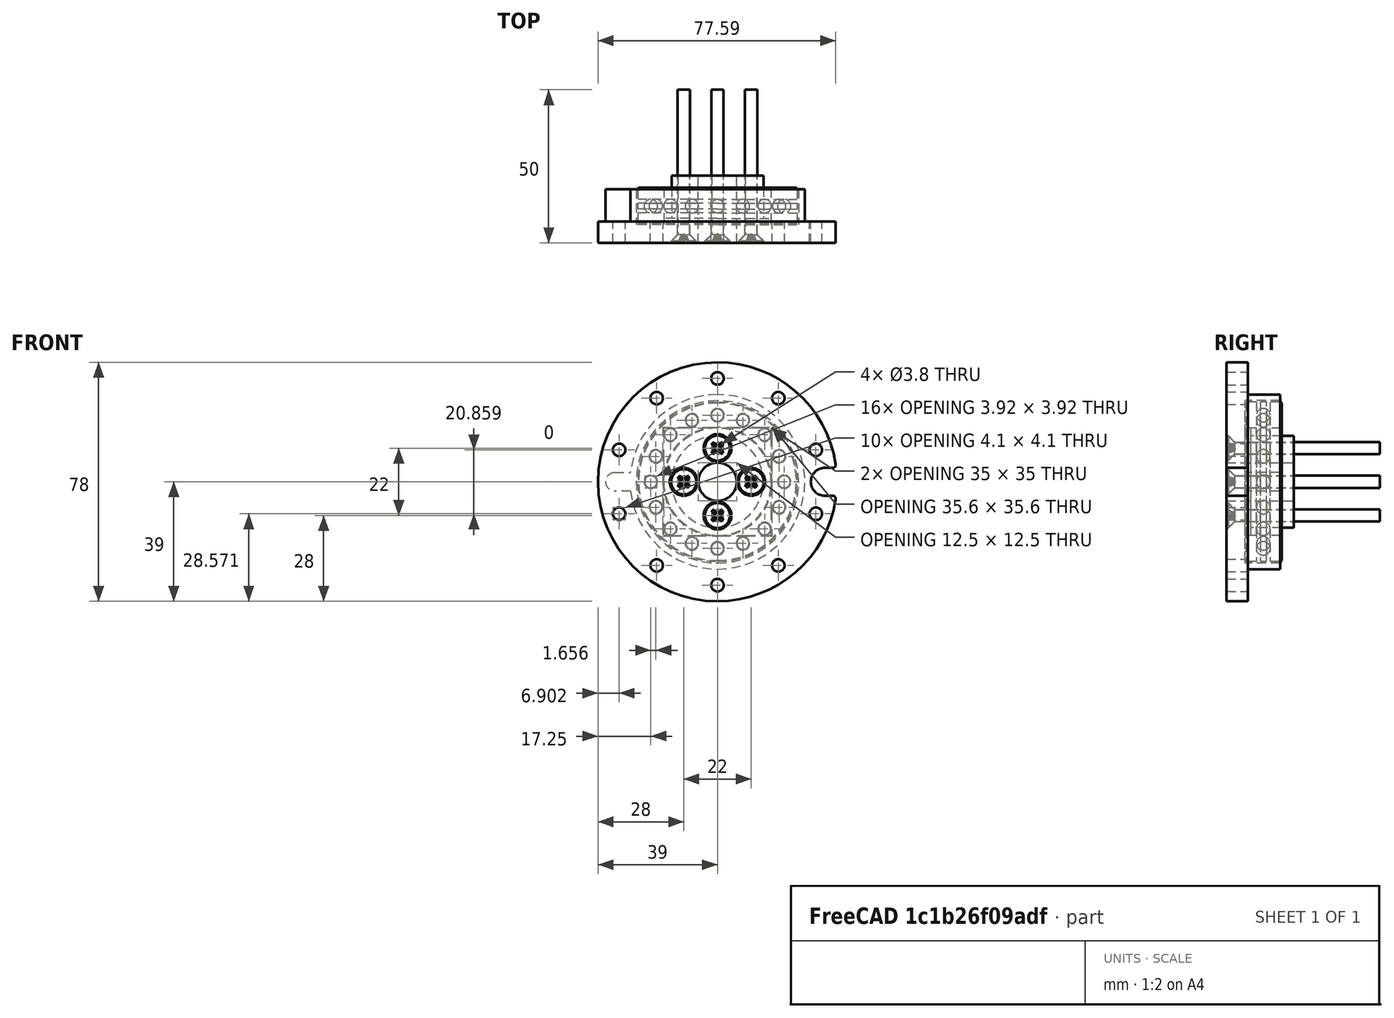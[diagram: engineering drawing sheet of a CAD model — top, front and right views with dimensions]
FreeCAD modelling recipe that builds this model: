
FCSTD DOCUMENT  (FreeCAD 0.19R)
Label: J3_a2p
License: All rights reserved
LicenseURL: http://en.wikipedia.org/wiki/All_rights_reserved
objects: Part::FeaturePython×6, App::FeaturePython×2, Spreadsheet::Sheet×2
note: 6 computed .brp shape members not serialized (recipe doc carries the construction recipe); baked Part::Feature solids carry a one-line shape summary decoded from their .brp

FEATURE [Part::FeaturePython] b_J3_coupler_modified_001_  label="J3_coupler_modified_001"  # a2plus imported part (geometry in sourceFile) (typed FeaturePython)
  a2p_Version = V0.1
  fixedPosition = true
  muxInfo = <blob: 8182 chars omitted>
  objectType = a2pPart
  sourceFile = ./J3_coupler_modified.FCStd
  subassemblyImport = false
  timeLastImport = 1.62025e+09
  updateColors = true
FEATURE [Part::FeaturePython] b_Thrust_bearing_511071_001_  label="Thrust_bearing_511071_001"  # a2plus imported part (geometry in sourceFile) (typed FeaturePython)
  Placement = pos=(-1.28618e-06,6,-2.39441e-06) rot=(0,0,1;0rad)
  a2p_Version = V0.1
  fixedPosition = false
  muxInfo = <blob: 16793 chars omitted>
  objectType = a2pPart
  sourceFile = ./Thrust_bearing_51107.step
  subassemblyImport = false
  timeLastImport = 1.62025e+09
  updateColors = true
FEATURE [App::FeaturePython] circularEdge_001  label="circularEdge_001__J3_coupler_modified_001"  # a2plus constraint (typed FeaturePython)
  Object1 = b_Thrust_bearing_511071_001_
  Object2 = b_J3_coupler_modified_001_
  ParentTreeObject = -> b_Thrust_bearing_511071_001_
  SubElement1 = Edge18
  SubElement2 = Edge157
  Suppressed = false
  Type = circularEdge
  directionConstraint = 1
  lockRotation = false
  offset = 0
FEATURE [App::FeaturePython] circularEdge_001_mirror  label="circularEdge_001__Thrust_bearing_511071_001"  # a2plus constraint (typed FeaturePython)
  Object1 = b_Thrust_bearing_511071_001_
  Object2 = b_J3_coupler_modified_001_
  ParentTreeObject = -> b_J3_coupler_modified_001_
  SubElement1 = Edge18
  SubElement2 = Edge157
  Suppressed = false
  Type = circularEdge
  directionConstraint = 1
  lockRotation = false
  offset = 0
FEATURE [Part::FeaturePython] Screw  label="M4x50-Screw"  # Fasteners workbench fastener (typed FeaturePython)
  Placement = pos=(0,-1.7e-15,-11) rot=(1,0,0;1.5708rad)
  baseObject = -> b_J3_coupler_modified_001_ [Edge46]
  diameter = 6
  invert = false
  length = 12
  lengthCustom = 50
  matchOuter = false
  offset = 0
  thread = false
  type = 35
FEATURE [Part::FeaturePython] Screw001  label="M4x50-Screw001"  # Fasteners workbench fastener (typed FeaturePython)
  Placement = pos=(-11,-1.7e-15,1.556e-13) rot=(1,0,0;1.5708rad)
  baseObject = -> b_J3_coupler_modified_001_ [Edge44]
  diameter = 6
  invert = false
  length = 12
  lengthCustom = 50
  matchOuter = false
  offset = 0
  thread = false
  type = 35
FEATURE [Part::FeaturePython] Screw002  label="M4x50-Screw002"  # Fasteners workbench fastener (typed FeaturePython)
  Placement = pos=(11,-1.7e-15,3.84e-14) rot=(1,0,0;1.5708rad)
  baseObject = -> b_J3_coupler_modified_001_ [Edge47]
  diameter = 6
  invert = false
  length = 12
  lengthCustom = 50
  matchOuter = false
  offset = 0
  thread = false
  type = 35
FEATURE [Part::FeaturePython] Screw003  label="M4x50-Screw003"  # Fasteners workbench fastener (typed FeaturePython)
  Placement = pos=(3.086e-13,-1.7e-15,11) rot=(1,0,0;1.5708rad)
  baseObject = -> b_J3_coupler_modified_001_ [Edge39]
  diameter = 6
  invert = false
  length = 12
  lengthCustom = 50
  matchOuter = false
  offset = 0
  thread = false
  type = 35
FEATURE [Spreadsheet::Sheet] Fasteners_BOM
  cells = A1=Type; B1=Qty; A2=ISO7046 Screw M4x50; B2=4
FEATURE [Spreadsheet::Sheet] _PARTSLIST_  label="#PARTSLIST#"
  cells = A1=POS; B1=QTY; C1=IDENTNO; D1=DESCRIPTION; E1=SUPPLIER; F1=SUPP.IDENTNO; G1=SUPP.DESCRIPTION; H1=(FILENAME); A2=1; B2=1; C2=*; D2=*; E2=*; F2=*; G2=*; H2=J3_coupler_modified.FCStd; A3=2; B3=1; C3=*; D3=*; E3=*; F3=*; G3=*; H3=Thrust_bearing_51107.step
